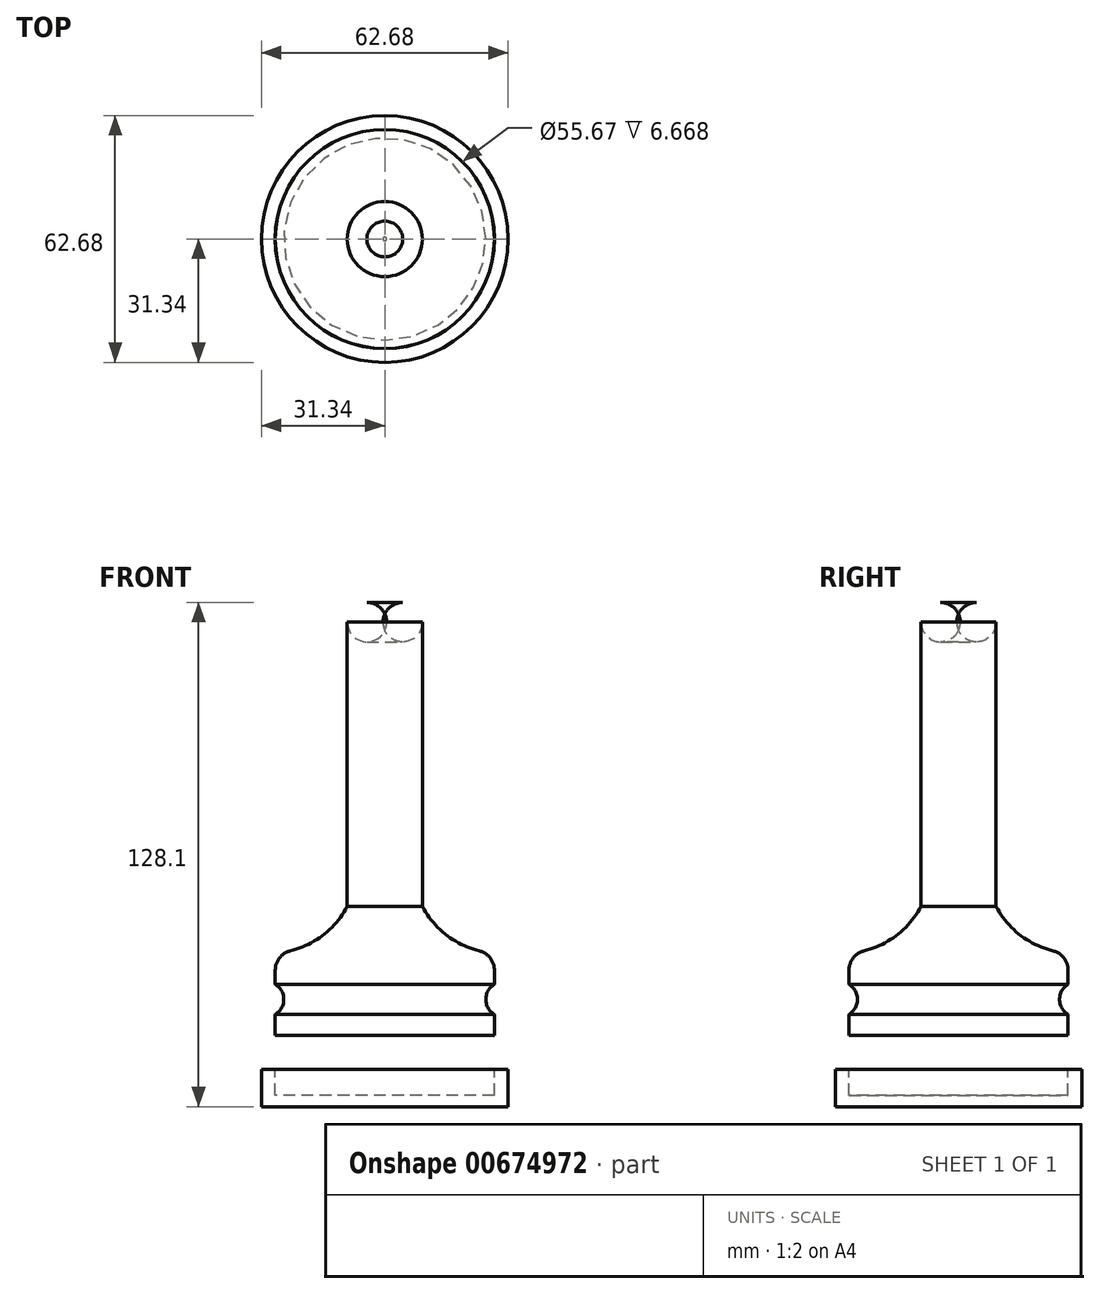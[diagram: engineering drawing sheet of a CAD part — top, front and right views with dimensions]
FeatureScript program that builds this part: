
annotation { "Feature Type Name" : "Feature", "Feature Type Description" : "" }
export const myFeature = defineFeature(function(context is Context, id is Id, definition is map)
    precondition{}
    {
        {
            var Q0;
            Q0=qCreatedBy(makeId("Front.planeOp"),FACE);
            var sketch = newSketch(context, id + "F0", { "sketchPlane" : qUnion([Q0])});
            skLineSegment(sketch, "E0", {"start": v(0, -58.96) * mm, "end": v(27.82, -58.96) * mm});
            skLineSegment(sketch, "E1", {"start": v(27.82, -58.96) * mm, "end": v(27.82, -38.07) * mm});
            skLineSegment(sketch, "E2", {"start": v(9.54, -26.22) * mm, "end": v(9.54, 51.04) * mm});
            skLineSegment(sketch, "E3", {"start": v(9.54, 51.04) * mm, "end": v(0, 51.04) * mm});
            skLineSegment(sketch, "E4", {"start": v(0, 51.04) * mm, "end": v(0, -58.96) * mm});
            skArc(sketch, "E5", {"start": v(9.54, -26.22) * mm, "mid": v(17.15, -34.5) * mm, "end": v(27.83, -38.07) * mm});
            skLineSegment(sketch, "E6", {"start": v(0, -74.2) * mm, "end": v(27.84, -74.2) * mm});
            skLineSegment(sketch, "E7", {"start": v(27.84, -74.2) * mm, "end": v(27.84, -67.53) * mm});
            skLineSegment(sketch, "E8", {"start": v(27.84, -67.53) * mm, "end": v(31.34, -67.53) * mm});
            skLineSegment(sketch, "E9", {"start": v(31.34, -67.53) * mm, "end": v(31.34, -77.06) * mm});
            skLineSegment(sketch, "E10", {"start": v(31.34, -77.06) * mm, "end": v(0, -77.06) * mm});
            skLineSegment(sketch, "E11", {"start": v(0, -77.06) * mm, "end": v(0, -74.2) * mm});
            skSolve(sketch);
        }
        {
            var Q0;
            Q0 = qSketchRegion(id + "F0", true);
            var Q1;
            Q1=sQuery(id+"F0.wireOp",EDGE,"E4");
            revolve(context, id + "F1", {"entities" : qUnion([Q0]), "axis" : qUnion([Q1]), "revolveType" : RevolveType.FULL});
        }
        {
            var Q0;
            Q0=qCreatedBy(makeId("Front.planeOp"),FACE);
            var sketch = newSketch(context, id + "F2", { "sketchPlane" : qUnion([Q0])});
            skCircle(sketch, "E12", {"center": v(30.13, -49.78) * mm, "radius": 4.45 * mm});
            skSolve(sketch);
        }
        {
            var Q0;
            Q0=makeQuery(id+"F1.opRevolve","SWEPT_EDGE",EDGE,{"disambiguationData":[OSD([sQuery(id+"F0.wireOp",EDGE,"E1"),sQuery(id+"F0.wireOp",EDGE,"E5")])]});
            fillet(context, id + "F3", {"entities" : qUnion([Q0]), "radius" : 5 * mm, "tangentPropagation" : true, "allowEdgeOverflow" : false});
        }
        {
            var Q0;
            Q0=makeQuery(id+"F1.opRevolve","SWEPT_EDGE",EDGE,{"disambiguationData":[OSD([sQuery(id+"F0.wireOp",EDGE,"E2"),sQuery(id+"F0.wireOp",EDGE,"E3")])]});
            fillet(context, id + "F4", {"entities" : qUnion([Q0]), "radius" : 5 * mm, "tangentPropagation" : true, "allowEdgeOverflow" : false});
        }
        {
            var Q0;
            Q0=makeQuery(id+"F2.imprint","IMPRINT",FACE,{"disambiguationData":[TD([[makeQuery(id+"F2.imprint","IMPRINT",EDGE,{"derivedFrom":sQuery(id+"F2.wireOp",EDGE,"E12")}),1.0]])]});
            var Q1;
            Q1=makeQuery(id+"F1.opRevolve","SWEPT_FACE",FACE,{"disambiguationData":[OSD([sQuery(id+"F0.wireOp",EDGE,"E1")])]});
            revolve(context, id + "F5", {"operationType" : NewBodyOperationType.REMOVE, "entities" : qUnion([Q0]), "axis" : qUnion([Q1]), "revolveType" : RevolveType.FULL, "oppositeDirection" : true});
        }
    });
